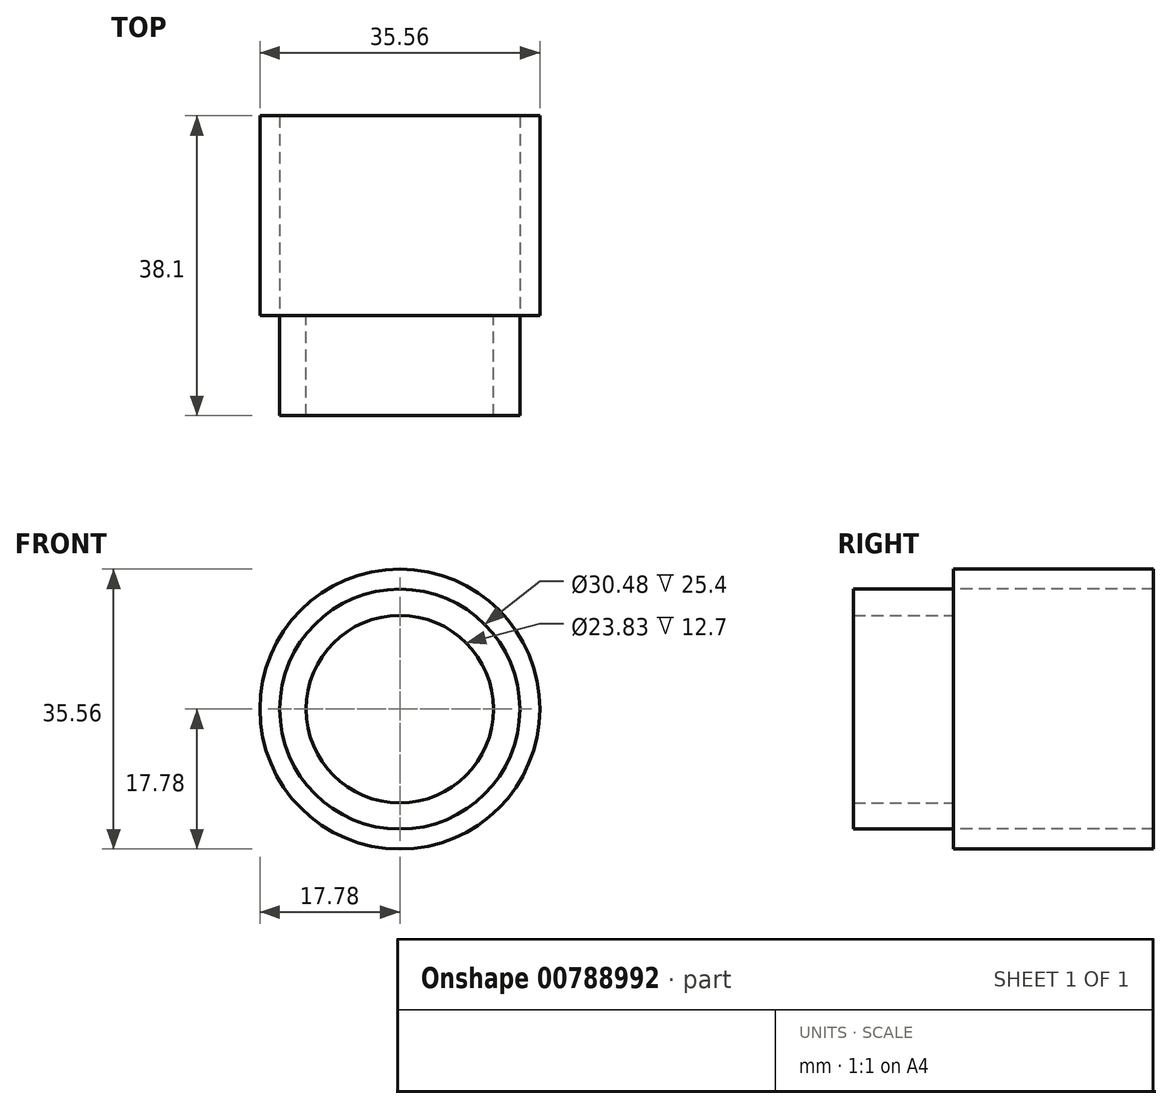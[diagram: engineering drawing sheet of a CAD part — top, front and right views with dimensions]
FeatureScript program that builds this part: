
annotation { "Feature Type Name" : "Feature", "Feature Type Description" : "" }
export const myFeature = defineFeature(function(context is Context, id is Id, definition is map)
    precondition{}
    {
        {
            var Q0;
            Q0=qCreatedBy(makeId("Front.planeOp"),FACE);
            var sketch = newSketch(context, id + "F0", { "sketchPlane" : qUnion([Q0])});
            skCircle(sketch, "E0", {"center": v(0, 0) * mm, "radius": 11.91 * mm});
            skCircle(sketch, "E1.0", {"center": v(0, 0) * mm, "radius": 15.24 * mm});
            skSolve(sketch);
        }
        {
            var Q0;
            Q0=makeQuery(id+"F0.imprint","IMPRINT",FACE,{"disambiguationData":[TD([[makeQuery(id+"F0.imprint","IMPRINT",EDGE,{"derivedFrom":sQuery(id+"F0.wireOp",EDGE,"E0")}),-1.0]])]});
            extrude(context, id + "F1", {"entities" : qUnion([Q0]), "depth" : 12.7 * mm, "offsetDistance" : 25.4 * mm});
        }
        {
            var Q0;
            Q0=qCreatedBy(makeId("Front.planeOp"),FACE);
            var sketch = newSketch(context, id + "F2", { "sketchPlane" : qUnion([Q0])});
            skCircle(sketch, "E2", {"center": v(0, 0) * mm, "radius": 12.88 * mm});
            skCircle(sketch, "E3.0", {"center": v(0, 0) * mm, "radius": 17.78 * mm});
            skCircle(sketch, "E4.0", {"center": v(0, 0) * mm, "radius": 15.24 * mm});
            skSolve(sketch);
        }
        {
            var Q0;
            Q0 = qSketchRegion(id + "F2", true);
            extrude(context, id + "F3", {"entities" : qUnion([Q0]), "oppositeDirection" : true, "depth" : 25.4 * mm, "offsetDistance" : 25.4 * mm});
        }
    });
